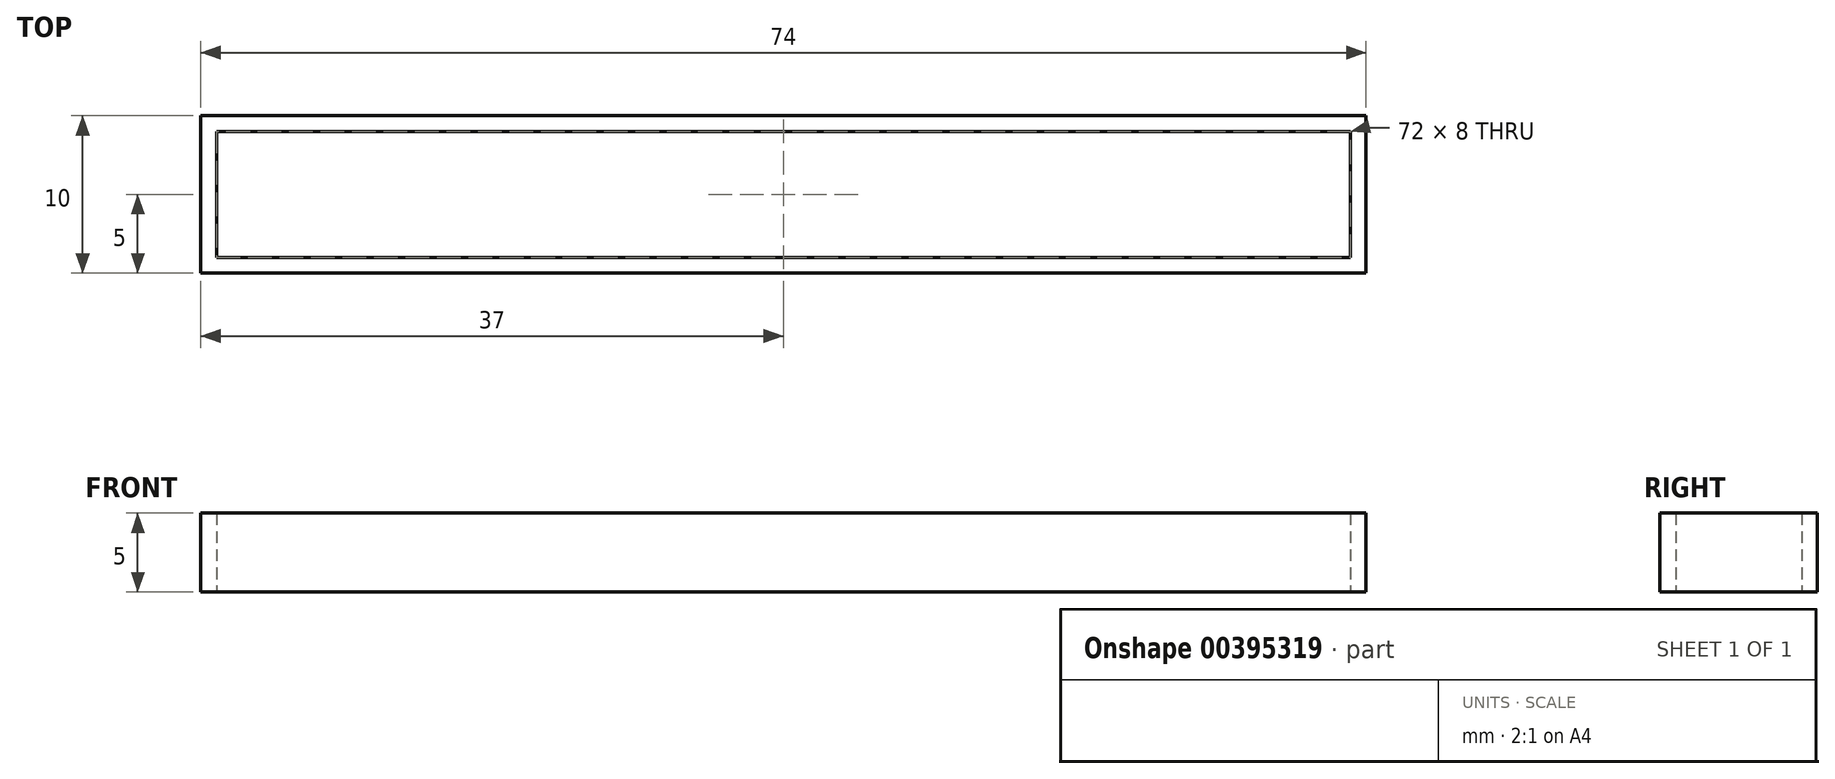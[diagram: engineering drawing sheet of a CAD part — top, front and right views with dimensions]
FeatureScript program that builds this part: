
annotation { "Feature Type Name" : "Feature", "Feature Type Description" : "" }
export const myFeature = defineFeature(function(context is Context, id is Id, definition is map)
    precondition{}
    {
        {
            var Q0;
            Q0=qCreatedBy(makeId("Front.planeOp"),FACE);
            var sketch = newSketch(context, id + "F0", { "sketchPlane" : qUnion([Q0])});
            skLineSegment(sketch, "E0.bottom", {"start": v(-37, 0) * mm, "end": v(37, 0) * mm});
            skLineSegment(sketch, "E0.top", {"start": v(-37, 5) * mm, "end": v(37, 5) * mm});
            skLineSegment(sketch, "E0.left", {"start": v(-37, 0) * mm, "end": v(-37, 5) * mm});
            skLineSegment(sketch, "E0.right", {"start": v(37, 0) * mm, "end": v(37, 5) * mm});
            skSolve(sketch);
        }
        {
            var Q0;
            Q0=makeQuery(id+"F0.imprint","IMPRINT",FACE,{"disambiguationData":[TD([[makeQuery(id+"F0.imprint","IMPRINT",EDGE,{"derivedFrom":sQuery(id+"F0.wireOp",EDGE,"E0.bottom")}),1.0]])]});
            extrude(context, id + "F1", {"entities" : qUnion([Q0]), "depth" : 10 * mm});
        }
        {
            var Q0;
            Q0=qCreatedBy(makeId("Top.planeOp"),FACE);
            var sketch = newSketch(context, id + "F2", { "sketchPlane" : qUnion([Q0])});
            skLineSegment(sketch, "E1.bottom", {"start": v(-36, -1) * mm, "end": v(36, -1) * mm});
            skLineSegment(sketch, "E1.top", {"start": v(-36, -9) * mm, "end": v(36, -9) * mm});
            skLineSegment(sketch, "E1.left", {"start": v(-36, -1) * mm, "end": v(-36, -9) * mm});
            skLineSegment(sketch, "E1.right", {"start": v(36, -1) * mm, "end": v(36, -9) * mm});
            skSolve(sketch);
        }
        {
            var Q0;
            Q0=makeQuery(id+"F2.imprint","IMPRINT",FACE,{"disambiguationData":[TD([[makeQuery(id+"F2.imprint","IMPRINT",EDGE,{"derivedFrom":sQuery(id+"F2.wireOp",EDGE,"E1.bottom")}),-1.0]])]});
            extrude(context, id + "F3", {"entities" : qUnion([Q0]), "operationType" : NewBodyOperationType.REMOVE, "depth" : 16.7 * mm});
        }
    });
